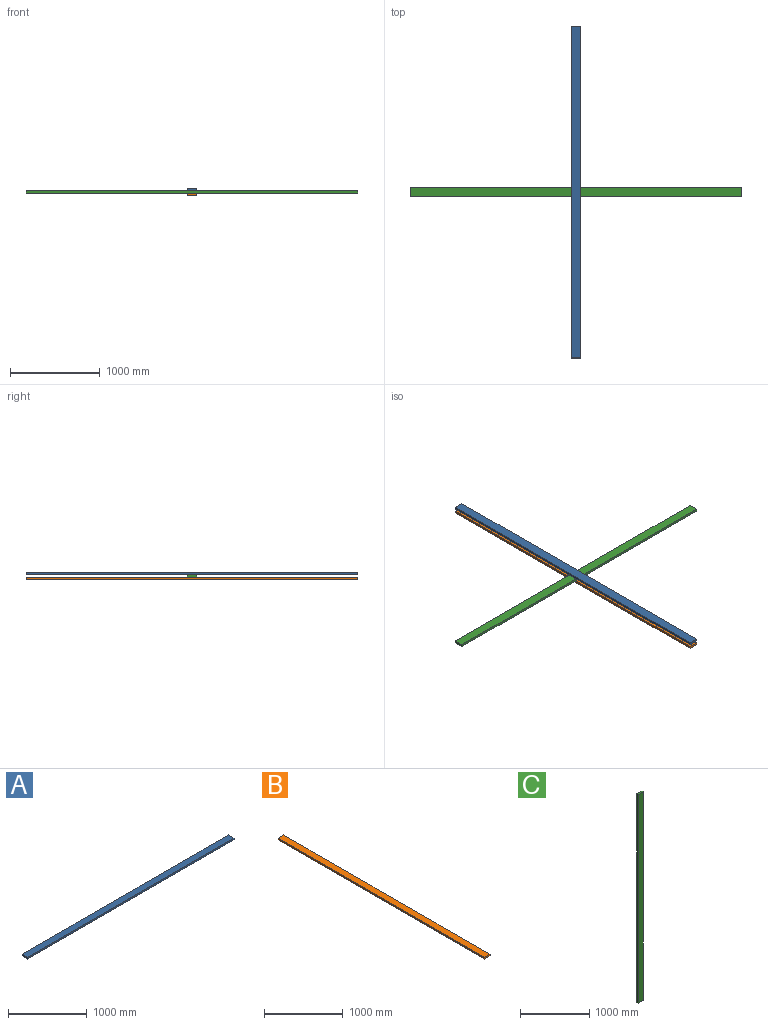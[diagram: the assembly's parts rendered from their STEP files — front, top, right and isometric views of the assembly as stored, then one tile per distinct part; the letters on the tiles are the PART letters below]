
ASSEMBLY  parts=3 mates=2
PART A: 6 faces, bbox 3694.2x102.6x25.7 mm
  f0: plane 3694.18x102.62mm, normal (0,0,-1), area 379081.6mm2, adj f1,f3,f4,f5
  f1: plane 3694.18x25.65mm, normal (0,1,0), area 94770.4mm2, adj f0,f2,f4,f5
  f2: plane 3694.18x102.62mm, normal (0,0,1), area 379081.6mm2, adj f1,f3,f4,f5
  f3: plane 3694.18x25.65mm, normal (0,-1,0), area 94770.4mm2, adj f0,f2,f4,f5
  f4: plane 102.62x25.65mm, normal (1,0,0), area 2632.5mm2, adj f0,f1,f2,f3
  f5: plane 102.62x25.65mm, normal (-1,0,0), area 2632.5mm2, adj f0,f1,f2,f3
PART B: 6 faces, bbox 102.6x3694.2x25.7 mm
  f0: plane 3694.18x102.62mm, normal (0,0,-1), area 379081.6mm2, adj f1,f3,f4,f5
  f1: plane 3694.18x25.65mm, normal (1,0,0), area 94770.4mm2, adj f0,f2,f4,f5
  f2: plane 3694.18x102.62mm, normal (0,0,1), area 379081.6mm2, adj f1,f3,f4,f5
  f3: plane 3694.18x25.65mm, normal (-1,0,0), area 94770.4mm2, adj f0,f2,f4,f5
  f4: plane 102.62x25.65mm, normal (0,-1,0), area 2632.5mm2, adj f0,f1,f2,f3
  f5: plane 102.62x25.65mm, normal (0,1,0), area 2632.5mm2, adj f0,f1,f2,f3
PART C: 6 faces, bbox 102.6x25.7x3694.2 mm
  f0: plane 3694.18x102.62mm, normal (0,-1,0), area 379081.6mm2, adj f1,f3,f4,f5
  f1: plane 3694.18x25.65mm, normal (1,0,0), area 94770.4mm2, adj f0,f2,f4,f5
  f2: plane 3694.18x102.62mm, normal (0,1,0), area 379081.6mm2, adj f1,f3,f4,f5
  f3: plane 3694.18x25.65mm, normal (-1,0,0), area 94770.4mm2, adj f0,f2,f4,f5
  f4: plane 102.62x25.65mm, normal (0,0,1), area 2632.5mm2, adj f0,f1,f2,f3
  f5: plane 102.62x25.65mm, normal (0,0,-1), area 2632.5mm2, adj f0,f1,f2,f3
PLACE A rot(axis=(0.71,0.71,0),180deg) t=(513.83,-3768.87,-571.98)mm
PLACE B t=(483.3,-74.69,-728.96)mm
PLACE C rot(axis=(-0.58,-0.58,0.58),120deg) t=(2531.65,-2010.02,-573.11)mm
MATE fastened C.f2 <-> B.f2  axis (0,0,-1) through (684.56,-1921.78,-680.25)mm
MATE fastened C.f0 <-> A.f2  axis (0,0,1) through (684.56,-1921.78,-654.59)mm
